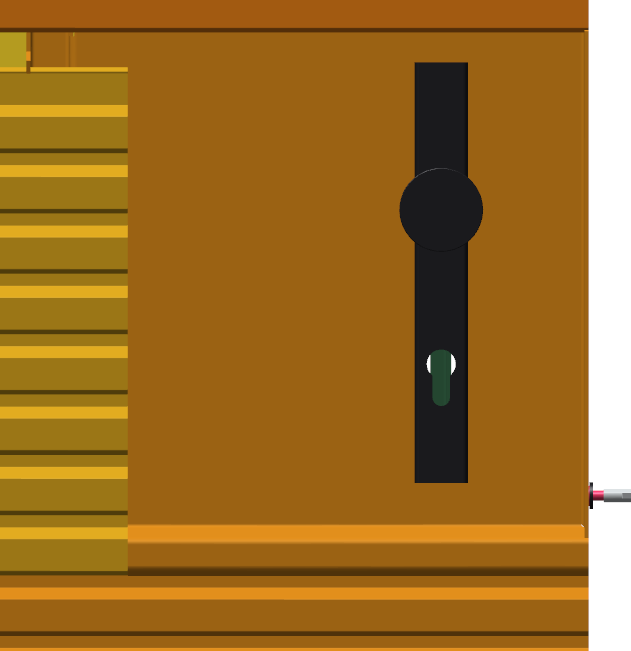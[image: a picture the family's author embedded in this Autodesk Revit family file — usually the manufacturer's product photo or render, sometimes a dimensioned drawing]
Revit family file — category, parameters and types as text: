
# Revit family: NLRS_31_DO_WB_HS50R enkele deur-AV_jazo_jazo
name_source: partatom
category: Doors
units: mm (PartAtom-declared; Revit-internal decimal feet)

## family parameters
Always vertical = Yes
Cut with Voids When Loaded = No
Host = Wall
OmniClass Number = 23.30.10.00
OmniClass Title = Doors
Room Calculation Point = No
Shared = No

## types (1)
- TYPE CATALOG
    Analytic Construction = <None>
    Assembly Code = 23.30.10.00
    Construction Type = Voor specificaties of mogelijkheden, neem contact op.
    Define Thermal Properties by = User Defined
    Description = HS50R enkele deur
    Function = Exterior
    Height = 2000 mm  [stored 6.56168 ft]
    JAZO_C_aluminium kozijn = No
    JAZO_C_calculatie_01 = 36 mm
    JAZO_C_calculatie_02 = 512 mm  [stored 1.67979 ft]
    JAZO_C_calculatie_03 = -83 mm
    JAZO_C_dagmaat breedte = 860 mm
    JAZO_C_dagmaat hoogte = 1860 mm
    JAZO_C_forster presto kozijn = Yes
    JAZO_C_materiaal aluminium kozijn = <By Category>
    JAZO_C_materiaal aluminium planken = <By Category>
    JAZO_C_materiaal beslag = <By Category>
    JAZO_C_materiaal forster presto deurprofiel = <By Category>
    JAZO_C_materiaal forster presto kozijn = <By Category>
    JAZO_C_materiaal forster presto sandwichpaneel = <By Category>
    JAZO_C_materiaal scharnier = <By Category>
    JAZO_C_materiaal schoep = <By Category>
    JAZO_C_niet ventilerend = Yes
    JAZO_C_opbouwrooster HS50R = Yes
    JAZO_C_paniekfunctie = No
    JAZO_C_ventilerend = No
    MAX HEIGHT = 3000 mm  [stored 9.84252 ft]
    MAX WIDTH = 1500 mm  [stored 4.92126 ft]
    MIN HEIGHT = 1850 mm  [stored 6.06955 ft]
    MIN WIDTH = 850 mm  [stored 2.78871 ft]
    Manufacturer = JAZO Zevenaar bv
    Model = HS50R enkele deur
    NLRS_C_aantal_01 = 2
    NLRS_C_aantal_02 = 8
    NLRS_C_brandwerend = No
    NLRS_C_breedte = 1000 mm  [stored 3.28084 ft]
    NLRS_C_breedte_01 = 1010 mm  [stored 3.31365 ft]
    NLRS_C_breedte_max = 1500 mm  [stored 4.92126 ft]
    NLRS_C_breedte_min = 850 mm  [stored 2.78871 ft]
    NLRS_C_content_datum gewijzigd = 7-11-2022
    NLRS_C_content_datum uitgifte = 17-8-2022
    NLRS_C_content_provider = JAZO Zevenaar bv
    NLRS_C_content_revit versie = REVIT 2020.2
    NLRS_C_content_versie = 2.5
    NLRS_C_diepte = 50 mm  [stored 0.164042 ft]
    NLRS_C_diepte_01 = 133 mm  [stored 0.436352 ft]
    NLRS_C_diepte_02 = 50 mm  [stored 0.164042 ft]
    NLRS_C_geluidwering Rw = Voor specificaties of mogelijkheden, neem contact op.
    NLRS_C_hoogte = 2000 mm  [stored 6.56168 ft]
    NLRS_C_hoogte_01 = 2010 mm
    NLRS_C_hoogte_max = 3000 mm  [stored 9.84252 ft]
    NLRS_C_hoogte_min = 1850 mm  [stored 6.06955 ft]
    NLRS_C_inbraakwerend = No
    NLRS_C_lengte_01 = 119 mm  [stored 0.39042 ft]
    NLRS_C_lengte_02 = 512 mm  [stored 1.67979 ft]
    NLRS_C_leverancier_adres = Handelsdwarsstraat 10
    NLRS_C_leverancier_bedrijfsnaam = JAZO Zevenaar bv
    NLRS_C_leverancier_plaats = Zevenaar
    NLRS_C_leverancier_postcode = 6905 DJ
    NLRS_C_leverancier_telefoonnummer = +31 316 - 59 29 11
    NLRS_C_leverancier_url = www.jazo.com
    NLRS_C_merk = Voor specificaties of mogelijkheden, neem contact op.
    NLRS_C_offset = 83 mm
    NLRS_C_offset_01 = 0 mm  [stored 0 ft]
    NLRS_C_offset_02 = 36 mm
    NLRS_C_rookwerendheid = Voor specificaties of mogelijkheden, neem contact op.
    NLRS_C_stelruimte = 5 mm  [stored 0.0164042 ft]
    NLRS_C_vluchtroute = Voor specificaties of mogelijkheden, neem contact op.
    NLRS_C_weerstandsklasse = Voor specificaties of mogelijkheden, neem contact op.
    NLRS_C_zelfsluitend = No
    Negge = 83 mm
    Rough Height = 2010 mm
    Rough Width = 1010 mm  [stored 3.31365 ft]
    Thickness = 50 mm  [stored 0.164042 ft]
    URL = www.jazo.com
    Wall Closure = By host
    Width = 1000 mm  [stored 3.28084 ft]

note: [stored X ft] marks values corroborated as IEEE doubles in the binary element streams (Revit-internal decimal feet)

## geometry (parser evidence)
native form markers: Sweep x43
no freeform markers — native parametric forms only
